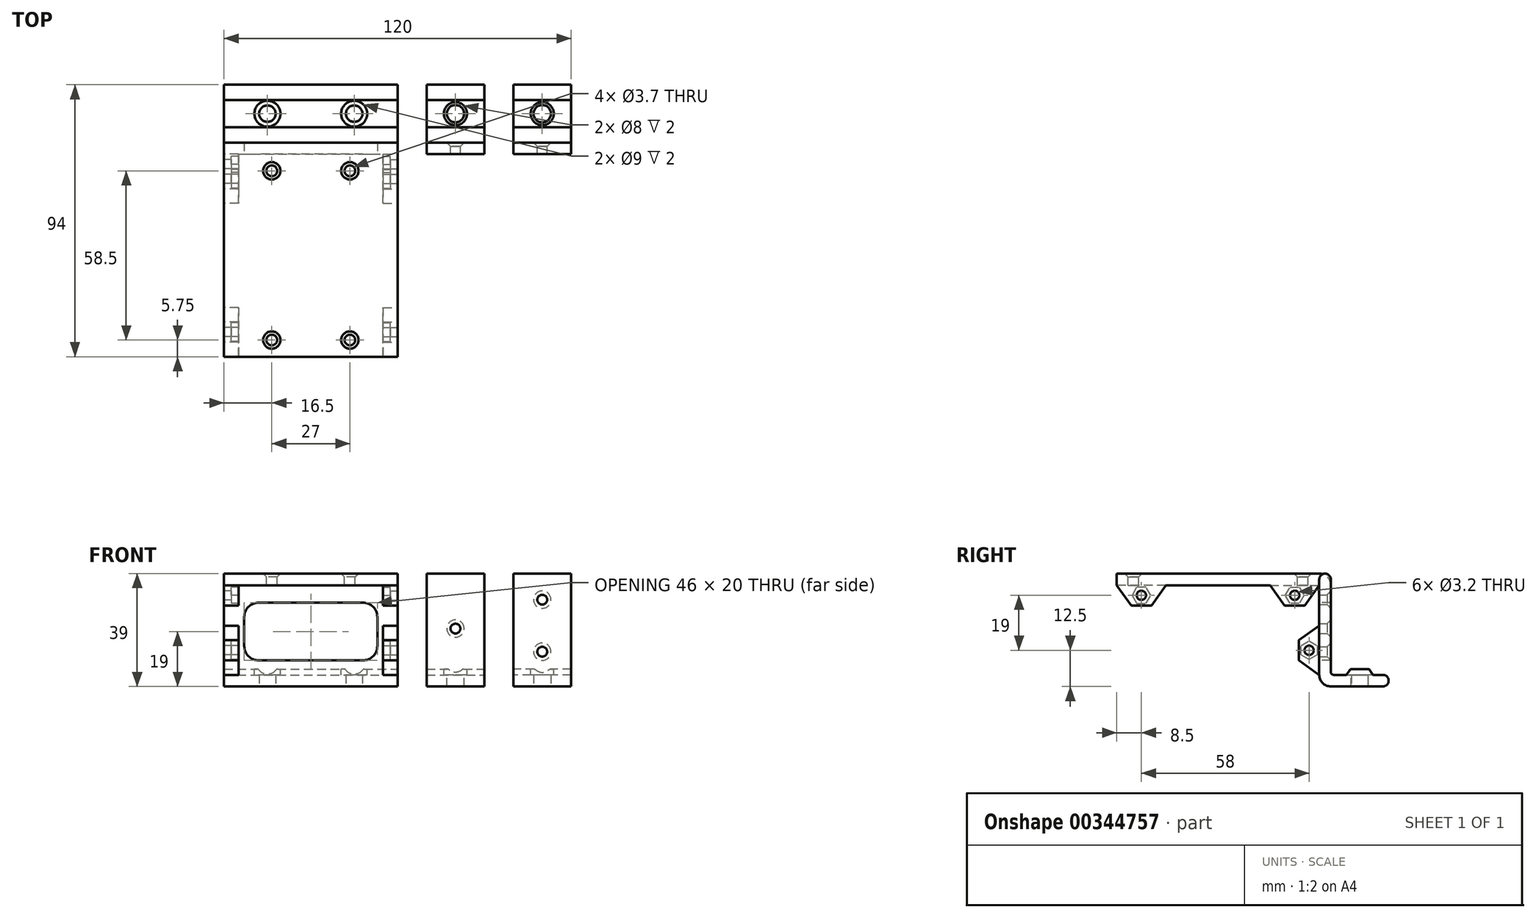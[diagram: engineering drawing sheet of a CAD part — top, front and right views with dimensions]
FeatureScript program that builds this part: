
annotation { "Feature Type Name" : "Feature", "Feature Type Description" : "" }
export const myFeature = defineFeature(function(context is Context, id is Id, definition is map)
    precondition{}
    {
        {
            var Q0;
            Q0=qCreatedBy(makeId("Right.planeOp"),FACE);
            var sketch = newSketch(context, id + "F0", { "sketchPlane" : qUnion([Q0])});
            skLineSegment(sketch, "E0", {"start": v(1, 0) * mm, "end": v(18, 0) * mm});
            skLineSegment(sketch, "E1", {"start": v(0, 1) * mm, "end": v(0, 33) * mm});
            skLineSegment(sketch, "E2.0", {"start": v(-4, 0) * mm, "end": v(-4, 33) * mm});
            skLineSegment(sketch, "E3.0", {"start": v(0, -4) * mm, "end": v(18, -4) * mm});
            skPoint(sketch, "E4.visualSharp", {"position": v(0, 0) * mm});
            skArc(sketch, "E4.filletArc", {"start": v(0, 1) * mm, "mid": v(0.3, 0.3) * mm, "end": v(1, 0) * mm});
            skArc(sketch, "E5", {"start": v(-4, 0) * mm, "mid": v(-2.83, -2.83) * mm, "end": v(0, -4) * mm});
            skLineSegment(sketch, "E6", {"start": v(31.11, 0) * mm, "end": v(-13.26, 0) * mm, "construction": true});
            skLineSegment(sketch, "E7", {"start": v(0, 49.75) * mm, "end": v(0, -11.4) * mm, "construction": true});
            skLineSegment(sketch, "E8", {"start": v(20, -2) * mm, "end": v(20, -2) * mm});
            skPoint(sketch, "E9.visualSharp", {"position": v(20, 0) * mm});
            skArc(sketch, "E9.filletArc", {"start": v(20, -2) * mm, "mid": v(19.41, -0.59) * mm, "end": v(18, 0) * mm});
            skPoint(sketch, "E10.visualSharp", {"position": v(20, -4) * mm});
            skArc(sketch, "E10.filletArc", {"start": v(18, -4) * mm, "mid": v(19.41, -3.41) * mm, "end": v(20, -2) * mm});
            skLineSegment(sketch, "E11", {"start": v(-2, 35) * mm, "end": v(-2, 35) * mm});
            skPoint(sketch, "E12.visualSharp", {"position": v(-4, 35) * mm});
            skArc(sketch, "E12.filletArc", {"start": v(-2, 35) * mm, "mid": v(-3.41, 34.41) * mm, "end": v(-4, 33) * mm});
            skPoint(sketch, "E13.visualSharp", {"position": v(0, 35) * mm});
            skArc(sketch, "E13.filletArc", {"start": v(0, 33) * mm, "mid": v(-0.59, 34.41) * mm, "end": v(-2, 35) * mm});
            skLineSegment(sketch, "E14", {"start": v(14.65, 0) * mm, "end": v(13.3, 1.8) * mm});
            skLineSegment(sketch, "E15", {"start": v(12.9, 2) * mm, "end": v(10, 2) * mm});
            skLineSegment(sketch, "E16.MirrorCS", {"start": v(7.1, 2) * mm, "end": v(10, 2) * mm});
            skLineSegment(sketch, "E17.MirrorCS", {"start": v(5.35, 0) * mm, "end": v(6.7, 1.8) * mm});
            skPoint(sketch, "E18.visualSharp", {"position": v(13.15, 2) * mm});
            skArc(sketch, "E18.filletArc", {"start": v(13.3, 1.8) * mm, "mid": v(13.12, 1.95) * mm, "end": v(12.9, 2) * mm});
            skPoint(sketch, "E19.visualSharp", {"position": v(6.85, 2) * mm});
            skArc(sketch, "E19.filletArc", {"start": v(7.1, 2) * mm, "mid": v(6.88, 1.95) * mm, "end": v(6.7, 1.8) * mm});
            skSolve(sketch);
        }
        {
            var Q0;
            Q0 = qSketchRegion(id + "F0", true);
            extrude(context, id + "F1", {"entities" : qUnion([Q0]), "depth" : 20 * mm});
        }
        {
            var Q0;
            Q0=makeQuery(id+"F1.opExtrude","SWEPT_FACE",FACE,{"disambiguationData":[OSD([sQuery(id+"F0.wireOp",EDGE,"E3.0")])]});
            var sketch = newSketch(context, id + "F2", { "sketchPlane" : qUnion([Q0])});
            skLineSegment(sketch, "E20.0", {"start": v(20, 0) * mm, "end": v(0, 0) * mm, "construction": true});
            skLineSegment(sketch, "E21.0", {"start": v(20, -18) * mm, "end": v(0, -18) * mm, "construction": true});
            skLineSegment(sketch, "E22.0", {"start": v(20, 0) * mm, "end": v(20, -18) * mm, "construction": true});
            skLineSegment(sketch, "E23.0", {"start": v(0, 0) * mm, "end": v(0, -18) * mm, "construction": true});
            skCircle(sketch, "E24", {"center": v(10, -10) * mm, "radius": 3 * mm});
            skSolve(sketch);
        }
        {
            var Q0;
            Q0=makeQuery(id+"F2.imprint","IMPRINT",FACE,{"disambiguationData":[TD([[makeQuery(id+"F2.imprint","IMPRINT",EDGE,{"derivedFrom":sQuery(id+"F2.wireOp",EDGE,"E24")}),1.0]])]});
            extrude(context, id + "F3", {"entities" : qUnion([Q0]), "operationType" : NewBodyOperationType.REMOVE, "endBound" : BoundingType.UP_TO_NEXT, "oppositeDirection" : true, "depth" : 25 * mm});
        }
        {
            var Q0;
            {var subQ0=sQuery(id+"F0.wireOp",EDGE,"E19.filletArc");var subQ1=sQuery(id+"F0.wireOp",EDGE,"E18.filletArc");var subQ2=sQuery(id+"F0.wireOp",EDGE,"E16.MirrorCS");var subQ3=sQuery(id+"F0.wireOp",EDGE,"E15");Q0=makeQuery(id+"F3.boolean.opBoolean","SPLIT",FACE,{"disambiguationData":[TD([makeQuery(id+"F1.opExtrude","CAP_FACE",FACE,{"disambiguationData":[OSD([sQuery(id+"F0.wireOp",EDGE,"E0"),sQuery(id+"F0.wireOp",EDGE,"E1"),sQuery(id+"F0.wireOp",EDGE,"E2.0"),sQuery(id+"F0.wireOp",EDGE,"E3.0"),sQuery(id+"F0.wireOp",EDGE,"E4.filletArc"),sQuery(id+"F0.wireOp",EDGE,"E5"),sQuery(id+"F0.wireOp",EDGE,"E9.filletArc"),sQuery(id+"F0.wireOp",EDGE,"E10.filletArc"),sQuery(id+"F0.wireOp",EDGE,"E12.filletArc"),sQuery(id+"F0.wireOp",EDGE,"E13.filletArc"),sQuery(id+"F0.wireOp",EDGE,"E14"),subQ3,subQ2,sQuery(id+"F0.wireOp",EDGE,"E17.MirrorCS"),subQ1,subQ0])],"isStart":false})])],"derivedFrom":makeQuery(id+"F1.opExtrude","SWEPT_FACE",FACE,{"disambiguationData":[OSD([subQ3,subQ2])]})});}
            var sketch = newSketch(context, id + "F4", { "sketchPlane" : qUnion([Q0])});
            skPoint(sketch, "E25.0", {"position": v(10, 10) * mm});
            skCircle(sketch, "E26", {"center": v(10, 10) * mm, "radius": 4 * mm});
            skSolve(sketch);
        }
        {
            var Q0;
            Q0=makeQuery(id+"F1.opExtrude","SWEPT_FACE",FACE,{"disambiguationData":[OSD([sQuery(id+"F0.wireOp",EDGE,"E2.0")])]});
            var sketch = newSketch(context, id + "F5", { "sketchPlane" : qUnion([Q0])});
            skLineSegment(sketch, "E27", {"start": v(0, 35) * mm, "end": v(20, 35) * mm, "construction": true});
            skLineSegment(sketch, "E28.0", {"start": v(0, 0) * mm, "end": v(0, 33) * mm, "construction": true});
            skCircle(sketch, "E29", {"center": v(10, 26) * mm, "radius": 1.85 * mm});
            skLineSegment(sketch, "E30.0", {"start": v(20, 0) * mm, "end": v(0, 0) * mm, "construction": true});
            skCircle(sketch, "E31", {"center": v(10, 8) * mm, "radius": 1.85 * mm});
            skSolve(sketch);
        }
        {
            var Q0;
            Q0=makeQuery(id+"F1.opExtrude","SWEPT_FACE",FACE,{"disambiguationData":[OSD([sQuery(id+"F0.wireOp",EDGE,"E1")])]});
            var sketch = newSketch(context, id + "F6", { "sketchPlane" : qUnion([Q0])});
            skPoint(sketch, "E32.0", {"position": v(-10, 26) * mm});
            skPoint(sketch, "E33.0", {"position": v(-10, 8) * mm});
            skSolve(sketch);
        }
        {
            var Q0;
            Q0=sQuery(id+"F6.wireOp",VERTEX,"E32.0");
            var Q1;
            Q1=sQuery(id+"F6.wireOp",VERTEX,"E33.0");
            var Q2;
            Q2=makeQuery(id+"F1.opExtrude","SWEPT_BODY",BODY,{"disambiguationData":[OSD([sQuery(id+"F0.wireOp",EDGE,"E0"),sQuery(id+"F0.wireOp",EDGE,"E1"),sQuery(id+"F0.wireOp",EDGE,"E2.0"),sQuery(id+"F0.wireOp",EDGE,"E3.0"),sQuery(id+"F0.wireOp",EDGE,"E4.filletArc"),sQuery(id+"F0.wireOp",EDGE,"E5"),sQuery(id+"F0.wireOp",EDGE,"E9.filletArc"),sQuery(id+"F0.wireOp",EDGE,"E10.filletArc"),sQuery(id+"F0.wireOp",EDGE,"E12.filletArc"),sQuery(id+"F0.wireOp",EDGE,"E13.filletArc")])]});
            hole(context, id + "F7", {"style" : HoleStyle.C_SINK, "endStyle" : HoleEndStyle.BLIND, "holeDiameter" : 3.4 * mm, "cSinkDiameter" : 6 * mm, "cSinkAngle" : 90 * degree, "holeDepth" : 12 * mm, "isTappedThrough" : true, "tappedDepth" : 12 * mm, "tapClearance" : 3, "locations" : qUnion([Q0, Q1]), "scope" : qUnion([Q2])});
        }
        {
            var Q0;
            Q0=qCreatedBy(makeId("Right.planeOp"),FACE);
            cPlane(context, id + "F8", {"entities" : qUnion([Q0]), "cplaneType" : CPlaneType.OFFSET, "offset" : 10 * mm, "oppositeDirection" : true, "width" : 150 * mm, "height" : 150 * mm});
        }
        {
            var Q0;
            Q0=qCreatedBy(id+"F8.planeOp",FACE);
            var sketch = newSketch(context, id + "F9", { "sketchPlane" : qUnion([Q0])});
            skPoint(sketch, "E34.0", {"position": v(-0.59, 34.41) * mm});
            skLineSegment(sketch, "E35.0", {"start": v(0, 1) * mm, "end": v(0, 33) * mm});
            skArc(sketch, "E35.1", {"start": v(0, 33) * mm, "mid": v(-0.59, 34.41) * mm, "end": v(-2, 35) * mm});
            skPoint(sketch, "E35.2", {"position": v(-4, 33) * mm});
            skLineSegment(sketch, "E35.3", {"start": v(-4, 0) * mm, "end": v(-4, 33) * mm});
            skArc(sketch, "E35.4", {"start": v(-2, 35) * mm, "mid": v(-3.41, 34.41) * mm, "end": v(-4, 33) * mm});
            skPoint(sketch, "E35.5", {"position": v(-3.41, 34.41) * mm});
            skLineSegment(sketch, "E36.0", {"start": v(1, 0) * mm, "end": v(18, 0) * mm});
            skPoint(sketch, "E37.0", {"position": v(19.41, -0.59) * mm});
            skPoint(sketch, "E38.0", {"position": v(19.41, -3.41) * mm});
            skArc(sketch, "E39.0", {"start": v(20, -2) * mm, "mid": v(19.41, -0.59) * mm, "end": v(18, 0) * mm});
            skArc(sketch, "E40.0", {"start": v(18, -4) * mm, "mid": v(19.41, -3.41) * mm, "end": v(20, -2) * mm});
            skLineSegment(sketch, "E41.0", {"start": v(0, -4) * mm, "end": v(18, -4) * mm});
            skArc(sketch, "E42.0", {"start": v(-4, 0) * mm, "mid": v(-2.83, -2.83) * mm, "end": v(0, -4) * mm});
            skArc(sketch, "E43.0", {"start": v(0, 1) * mm, "mid": v(0.3, 0.3) * mm, "end": v(1, 0) * mm});
            skLineSegment(sketch, "E44.0", {"start": v(14.65, 0) * mm, "end": v(13.3, 1.8) * mm});
            skArc(sketch, "E45.0", {"start": v(13.3, 1.8) * mm, "mid": v(13.12, 1.95) * mm, "end": v(12.9, 2) * mm});
            skLineSegment(sketch, "E46.0", {"start": v(12.9, 2) * mm, "end": v(10, 2) * mm});
            skLineSegment(sketch, "E47.0", {"start": v(7.1, 2) * mm, "end": v(10, 2) * mm});
            skArc(sketch, "E48.0", {"start": v(7.1, 2) * mm, "mid": v(6.88, 1.95) * mm, "end": v(6.7, 1.8) * mm});
            skLineSegment(sketch, "E49.0", {"start": v(5.35, 0) * mm, "end": v(6.7, 1.8) * mm});
            skSolve(sketch);
        }
        {
            var Q0;
            Q0=makeQuery(id+"F9.imprint","IMPRINT",FACE,{"disambiguationData":[TD([[makeQuery(id+"F9.imprint","IMPRINT",EDGE,{"derivedFrom":sQuery(id+"F9.wireOp",EDGE,"E35.0")}),1.0]])]});
            var Q1;
            {var subQ0=sQuery(id+"F9.wireOp",EDGE,"E44.0");Q1=makeQuery(id+"F9.imprint","IMPRINT",FACE,{"disambiguationData":[TD([[makeQuery(id+"F9.imprint","IMPRINT",EDGE,{"derivedFrom":subQ0}),1.0]])]});}
            extrude(context, id + "F10", {"entities" : qUnion([Q0, Q1]), "oppositeDirection" : true, "depth" : 20 * mm});
        }
        {
            var Q0;
            Q0=makeQuery(id+"F10.opExtrude","SWEPT_FACE",FACE,{"disambiguationData":[OSD([sQuery(id+"F9.wireOp",EDGE,"E36.0")])]});
            var sketch = newSketch(context, id + "F11", { "sketchPlane" : qUnion([Q0])});
            skCircle(sketch, "E50", {"center": v(-20, 10) * mm, "radius": 3 * mm});
            skLineSegment(sketch, "E51.0", {"start": v(-30, 0) * mm, "end": v(-10, 0) * mm, "construction": true});
            skSolve(sketch);
        }
        {
            var Q0;
            Q0=makeQuery(id+"F11.imprint","IMPRINT",FACE,{"disambiguationData":[TD([[makeQuery(id+"F11.imprint","IMPRINT",EDGE,{"derivedFrom":sQuery(id+"F11.wireOp",EDGE,"E50")}),1.0]])]});
            extrude(context, id + "F12", {"entities" : qUnion([Q0]), "operationType" : NewBodyOperationType.REMOVE, "endBound" : BoundingType.SYMMETRIC, "oppositeDirection" : true, "depth" : 25 * mm});
        }
        {
            var Q0;
            {var subQ0=sQuery(id+"F9.wireOp",EDGE,"E48.0");var subQ1=sQuery(id+"F9.wireOp",EDGE,"E47.0");var subQ2=sQuery(id+"F9.wireOp",EDGE,"E46.0");var subQ3=sQuery(id+"F9.wireOp",EDGE,"E45.0");Q0=makeQuery(id+"F12.boolean.opBoolean","SPLIT",FACE,{"disambiguationData":[TD([makeQuery(id+"F10.opExtrude","CAP_FACE",FACE,{"disambiguationData":[OSD([sQuery(id+"F9.wireOp",EDGE,"E35.0"),sQuery(id+"F9.wireOp",EDGE,"E35.1"),sQuery(id+"F9.wireOp",EDGE,"E35.3"),sQuery(id+"F9.wireOp",EDGE,"E35.4"),sQuery(id+"F9.wireOp",EDGE,"E36.0"),sQuery(id+"F9.wireOp",EDGE,"E39.0"),sQuery(id+"F9.wireOp",EDGE,"E40.0"),sQuery(id+"F9.wireOp",EDGE,"E41.0"),sQuery(id+"F9.wireOp",EDGE,"E42.0"),sQuery(id+"F9.wireOp",EDGE,"E43.0"),sQuery(id+"F9.wireOp",EDGE,"E44.0"),subQ3,subQ2,subQ1,subQ0,sQuery(id+"F9.wireOp",EDGE,"E49.0")])],"isStart":true})])],"derivedFrom":makeQuery(id+"F10.opExtrude","SWEPT_FACE",FACE,{"disambiguationData":[OSD([subQ2,subQ1])]})});}
            var sketch = newSketch(context, id + "F13", { "sketchPlane" : qUnion([Q0])});
            skPoint(sketch, "E52.0", {"position": v(-20, 10) * mm});
            skCircle(sketch, "E53", {"center": v(-20, 10) * mm, "radius": 4 * mm});
            skSolve(sketch);
        }
        {
            var Q0;
            Q0 = qSketchRegion(id + "F13", true);
            extrude(context, id + "F14", {"entities" : qUnion([Q0]), "operationType" : NewBodyOperationType.REMOVE, "oppositeDirection" : true, "depth" : 2 * mm});
        }
        {
            var Q0;
            Q0=makeQuery(id+"F10.opExtrude","SWEPT_FACE",FACE,{"disambiguationData":[OSD([sQuery(id+"F9.wireOp",EDGE,"E35.0")])]});
            var sketch = newSketch(context, id + "F15", { "sketchPlane" : qUnion([Q0])});
            skLineSegment(sketch, "E54.0", {"start": v(30, 0) * mm, "end": v(10, 0) * mm, "construction": true});
            skPoint(sketch, "E55", {"position": v(20, 16) * mm});
            skSolve(sketch);
        }
        {
            var Q0;
            Q0=sQuery(id+"F15.wireOp",VERTEX,"E55");
            var Q1;
            Q1=makeQuery(id+"F10.opExtrude","SWEPT_BODY",BODY,{"disambiguationData":[OSD([sQuery(id+"F9.wireOp",EDGE,"E35.0"),sQuery(id+"F9.wireOp",EDGE,"E35.1"),sQuery(id+"F9.wireOp",EDGE,"E35.3"),sQuery(id+"F9.wireOp",EDGE,"E35.4"),sQuery(id+"F9.wireOp",EDGE,"E36.0"),sQuery(id+"F9.wireOp",EDGE,"E39.0"),sQuery(id+"F9.wireOp",EDGE,"E40.0"),sQuery(id+"F9.wireOp",EDGE,"E41.0"),sQuery(id+"F9.wireOp",EDGE,"E42.0"),sQuery(id+"F9.wireOp",EDGE,"E43.0")])]});
            hole(context, id + "F16", {"style" : HoleStyle.C_SINK, "endStyle" : HoleEndStyle.BLIND, "holeDiameter" : 3.4 * mm, "cSinkDiameter" : 6 * mm, "cSinkAngle" : 90 * degree, "holeDepth" : 12 * mm, "isTappedThrough" : true, "tappedDepth" : 12 * mm, "tapClearance" : 3, "locations" : qUnion([Q0]), "scope" : qUnion([Q1])});
        }
        {
            var Q0;
            Q0=qCreatedBy(makeId("Right.planeOp"),FACE);
            cPlane(context, id + "F17", {"entities" : qUnion([Q0]), "cplaneType" : CPlaneType.OFFSET, "offset" : 40 * mm, "oppositeDirection" : true, "width" : 150 * mm, "height" : 150 * mm});
        }
        {
            var Q0;
            Q0=qCreatedBy(id+"F17.planeOp",FACE);
            var sketch = newSketch(context, id + "F18", { "sketchPlane" : qUnion([Q0])});
            skLineSegment(sketch, "E56.0.2", {"start": v(-4, 35) * mm, "end": v(-4, 0) * mm});
            skArc(sketch, "E56.0.3", {"start": v(-4, 0) * mm, "mid": v(-2.83, -2.83) * mm, "end": v(0, -4) * mm});
            skLineSegment(sketch, "E56.0.4", {"start": v(0, -4) * mm, "end": v(18, -4) * mm});
            skArc(sketch, "E56.0.5", {"start": v(18, -4) * mm, "mid": v(19.41, -3.41) * mm, "end": v(20, -2) * mm});
            skArc(sketch, "E56.0.6", {"start": v(20, -2) * mm, "mid": v(19.41, -0.59) * mm, "end": v(18, 0) * mm});
            skLineSegment(sketch, "E56.0.7", {"start": v(18, 0) * mm, "end": v(1, 0) * mm});
            skArc(sketch, "E56.0.8", {"start": v(1, 0) * mm, "mid": v(0.3, 0.3) * mm, "end": v(0, 1) * mm});
            skLineSegment(sketch, "E56.0.9", {"start": v(0, 1) * mm, "end": v(0, 35) * mm});
            skLineSegment(sketch, "E57", {"start": v(0, 35) * mm, "end": v(-4, 35) * mm});
            skLineSegment(sketch, "E58", {"start": v(10, -6.98) * mm, "end": v(10, 10.98) * mm, "construction": true});
            skPoint(sketch, "E58.startSnap0", {"position": v(10, -4) * mm});
            skLineSegment(sketch, "E59", {"start": v(14.65, 0) * mm, "end": v(13.3, 1.8) * mm});
            skLineSegment(sketch, "E60", {"start": v(12.9, 2) * mm, "end": v(10, 2) * mm});
            skLineSegment(sketch, "E61.MirrorCS", {"start": v(7.1, 2) * mm, "end": v(10, 2) * mm});
            skLineSegment(sketch, "E62.MirrorCS", {"start": v(5.35, 0) * mm, "end": v(6.7, 1.8) * mm});
            skPoint(sketch, "E63.visualSharp", {"position": v(13.15, 2) * mm});
            skArc(sketch, "E63.filletArc", {"start": v(13.3, 1.8) * mm, "mid": v(13.12, 1.95) * mm, "end": v(12.9, 2) * mm});
            skPoint(sketch, "E64.visualSharp", {"position": v(6.85, 2) * mm});
            skArc(sketch, "E64.filletArc", {"start": v(7.1, 2) * mm, "mid": v(6.88, 1.95) * mm, "end": v(6.7, 1.8) * mm});
            skSolve(sketch);
        }
        {
            var Q0;
            Q0=makeQuery(id+"F18.imprint","IMPRINT",FACE,{"disambiguationData":[TD([[makeQuery(id+"F18.imprint","IMPRINT",EDGE,{"derivedFrom":sQuery(id+"F18.wireOp",EDGE,"E56.0.2")}),1.0]])]});
            var Q1;
            {var subQ0=sQuery(id+"F18.wireOp",EDGE,"E59");Q1=makeQuery(id+"F18.imprint","IMPRINT",FACE,{"disambiguationData":[TD([[makeQuery(id+"F18.imprint","IMPRINT",EDGE,{"derivedFrom":subQ0}),1.0]])]});}
            extrude(context, id + "F19", {"entities" : qUnion([Q0, Q1]), "operationType" : NewBodyOperationType.ADD, "oppositeDirection" : true, "depth" : 60 * mm});
        }
        {
            var Q0;
            Q0=makeQuery(id+"F19.opExtrude","SWEPT_FACE",FACE,{"disambiguationData":[OSD([sQuery(id+"F18.wireOp",EDGE,"E57")])]});
            var sketch = newSketch(context, id + "F20", { "sketchPlane" : qUnion([Q0])});
            skLineSegment(sketch, "E65.0", {"start": v(-100, -4) * mm, "end": v(-40, -4) * mm});
            skLineSegment(sketch, "E66.top", {"start": v(-100, -74) * mm, "end": v(-40, -74) * mm});
            skLineSegment(sketch, "E66.left", {"start": v(-100, -4) * mm, "end": v(-100, -74) * mm});
            skLineSegment(sketch, "E66.right", {"start": v(-40, -4) * mm, "end": v(-40, -74) * mm});
            skSolve(sketch);
        }
        {
            var Q0;
            Q0 = qSketchRegion(id + "F20", true);
            extrude(context, id + "F21", {"entities" : qUnion([Q0]), "operationType" : NewBodyOperationType.ADD, "oppositeDirection" : true, "depth" : 4 * mm});
        }
        {
            var Q0;
            Q0=makeQuery(id+"F19.opExtrude","SWEPT_EDGE",EDGE,{"disambiguationData":[OSD([sQuery(id+"F18.wireOp",EDGE,"E56.0.9"),sQuery(id+"F18.wireOp",EDGE,"E57")])]});
            fillet(context, id + "F22", {"entities" : qUnion([Q0]), "radius" : 4 * mm, "tangentPropagation" : true, "allowEdgeOverflow" : false});
        }
        {
            var Q0;
            Q0=makeQuery(id+"F19.opExtrude","SWEPT_FACE",FACE,{"disambiguationData":[OSD([sQuery(id+"F18.wireOp",EDGE,"E56.0.4")])]});
            var sketch = newSketch(context, id + "F23", { "sketchPlane" : qUnion([Q0])});
            skLineSegment(sketch, "E67.0", {"start": v(-100, 0) * mm, "end": v(-100, -18) * mm, "construction": true});
            skLineSegment(sketch, "E68.0", {"start": v(-40, 0) * mm, "end": v(-40, -18) * mm, "construction": true});
            skPoint(sketch, "E69", {"position": v(-85, -10) * mm});
            skLineSegment(sketch, "E70", {"start": v(-70, -20) * mm, "end": v(-70, 0) * mm, "construction": true});
            skLineSegment(sketch, "E71", {"start": v(-70, -10) * mm, "end": v(-100, -10) * mm, "construction": true});
            skLineSegment(sketch, "E72", {"start": v(-40, -20) * mm, "end": v(-100, -20) * mm, "construction": true});
            skLineSegment(sketch, "E73", {"start": v(-100, -20) * mm, "end": v(-100, 0) * mm, "construction": true});
            skPoint(sketch, "E74.MirrorP", {"position": v(-55, -10) * mm});
            skSolve(sketch);
        }
        {
            var Q0;
            Q0=sQuery(id+"F23.wireOp",VERTEX,"E69");
            var Q1;
            Q1=sQuery(id+"F23.wireOp",VERTEX,"E74.MirrorP");
            var Q2;
            Q2=makeQuery(id+"F19.opExtrude","SWEPT_BODY",BODY,{"disambiguationData":[OSD([sQuery(id+"F18.wireOp",EDGE,"E56.0.2"),sQuery(id+"F18.wireOp",EDGE,"E56.0.3"),sQuery(id+"F18.wireOp",EDGE,"E56.0.4"),sQuery(id+"F18.wireOp",EDGE,"E56.0.5"),sQuery(id+"F18.wireOp",EDGE,"E56.0.6"),sQuery(id+"F18.wireOp",EDGE,"E56.0.7"),sQuery(id+"F18.wireOp",EDGE,"E56.0.8"),sQuery(id+"F18.wireOp",EDGE,"E56.0.9"),sQuery(id+"F18.wireOp",EDGE,"E57"),sQuery(id+"F18.wireOp",EDGE,"E59"),sQuery(id+"F18.wireOp",EDGE,"E60"),sQuery(id+"F18.wireOp",EDGE,"E61.MirrorCS"),sQuery(id+"F18.wireOp",EDGE,"E62.MirrorCS")])]});
            hole(context, id + "F24", {"style" : HoleStyle.SIMPLE, "endStyle" : HoleEndStyle.THROUGH, "holeDiameter" : 5.7 * mm, "isTappedThrough" : true, "tappedDepth" : 12 * mm, "tapClearance" : 3, "locations" : qUnion([Q0, Q1]), "scope" : qUnion([Q2])});
        }
        {
            var Q0;
            {var subQ4=makeQuery(id+"F24.hole-0.opRevolve","SWEPT_FACE",FACE,{"disambiguationData":[OSD([sQuery(id+"F24.hole-0.sketch.wireOp",EDGE,"core_line_2")])]});var subQ5=sQuery(id+"F18.wireOp",EDGE,"E61.MirrorCS");var subQ6=sQuery(id+"F18.wireOp",EDGE,"E60");Q0=makeQuery(id+"F24.hole-1.boolean.opBoolean","SPLIT",FACE,{"disambiguationData":[TD([makeQuery(id+"F24.hole-0.boolean.opBoolean","COPY",FACE,{"derivedFrom":subQ4})])],"derivedFrom":makeQuery(id+"F24.hole-0.boolean.opBoolean","SPLIT",FACE,{"disambiguationData":[TD([makeQuery(id+"F21.opExtrude","SWEPT_FACE",FACE,{"disambiguationData":[OSD([sQuery(id+"F20.wireOp",EDGE,"E66.right")])]})])],"derivedFrom":makeQuery(id+"F19.opExtrude","SWEPT_FACE",FACE,{"disambiguationData":[OSD([subQ6,subQ5])]})})});}
            var sketch = newSketch(context, id + "F25", { "sketchPlane" : qUnion([Q0])});
            skCircle(sketch, "E75.0", {"center": v(-85, 10) * mm, "radius": 2.85 * mm});
            skCircle(sketch, "E76.0", {"center": v(-55, 10) * mm, "radius": 2.85 * mm});
            skCircle(sketch, "E77", {"center": v(-85, 10) * mm, "radius": 4.5 * mm});
            skCircle(sketch, "E78", {"center": v(-55, 10) * mm, "radius": 4.5 * mm});
            skSolve(sketch);
        }
        {
            var Q0;
            {var subQ0=sQuery(id+"F25.wireOp",EDGE,"E75.0");Q0=makeQuery(id+"F25.imprint","IMPRINT",FACE,{"disambiguationData":[TD([[makeQuery(id+"F25.imprint","IMPRINT",EDGE,{"disambiguationData":[OD(1.0)],"derivedFrom":subQ0}),1.0]])]});}
            var Q1;
            {var subQ0=sQuery(id+"F25.wireOp",EDGE,"E77");var subQ1=makeQuery(id+"F19.opExtrude","SWEPT_EDGE",EDGE,{"disambiguationData":[OSD([sQuery(id+"F18.wireOp",EDGE,"E60"),sQuery(id+"F18.wireOp",EDGE,"E63.filletArc")])]});var subQ2=makeQuery(id+"F25.imprint","INTERSECT",VERTEX,{"disambiguationData":[OD(0.0)],"derivedFrom":[subQ1,subQ0]});Q1=makeQuery(id+"F25.imprint","IMPRINT",FACE,{"disambiguationData":[TD([[makeQuery(id+"F25.imprint","IMPRINT",EDGE,{"disambiguationData":[TD([[subQ2,1.0]])],"derivedFrom":subQ0}),1.0]])]});}
            var Q2;
            {var subQ0=sQuery(id+"F25.wireOp",EDGE,"E75.0");Q2=makeQuery(id+"F25.imprint","IMPRINT",FACE,{"disambiguationData":[TD([[makeQuery(id+"F25.imprint","IMPRINT",EDGE,{"disambiguationData":[OD(0.0)],"derivedFrom":subQ0}),-1.0]])]});}
            var Q3;
            {var subQ0=sQuery(id+"F25.wireOp",EDGE,"E76.0");Q3=makeQuery(id+"F25.imprint","IMPRINT",FACE,{"disambiguationData":[TD([[makeQuery(id+"F25.imprint","IMPRINT",EDGE,{"disambiguationData":[OD(0.0)],"derivedFrom":subQ0}),-1.0]])]});}
            var Q4;
            {var subQ0=sQuery(id+"F25.wireOp",EDGE,"E77");var subQ1=makeQuery(id+"F19.opExtrude","SWEPT_EDGE",EDGE,{"disambiguationData":[OSD([sQuery(id+"F18.wireOp",EDGE,"E61.MirrorCS"),sQuery(id+"F18.wireOp",EDGE,"E64.filletArc")])]});var subQ2=makeQuery(id+"F25.imprint","INTERSECT",VERTEX,{"disambiguationData":[OD(0.0)],"derivedFrom":[subQ1,subQ0]});Q4=makeQuery(id+"F25.imprint","IMPRINT",FACE,{"disambiguationData":[TD([[makeQuery(id+"F25.imprint","IMPRINT",EDGE,{"disambiguationData":[TD([[subQ2,-1.0]])],"derivedFrom":subQ0}),1.0]])]});}
            var Q5;
            Q5=makeQuery(id+"F25.imprint","IMPRINT",FACE,{"disambiguationData":[TD([[makeQuery(id+"F25.imprint","IMPRINT",EDGE,{"derivedFrom":sQuery(id+"F25.wireOp",EDGE,"E76.0")}),1.0]])]});
            var Q6;
            {var subQ0=sQuery(id+"F25.wireOp",EDGE,"E78");var subQ1=makeQuery(id+"F19.opExtrude","SWEPT_EDGE",EDGE,{"disambiguationData":[OSD([sQuery(id+"F18.wireOp",EDGE,"E61.MirrorCS"),sQuery(id+"F18.wireOp",EDGE,"E64.filletArc")])]});var subQ2=makeQuery(id+"F25.imprint","INTERSECT",VERTEX,{"disambiguationData":[OD(0.0)],"derivedFrom":[subQ1,subQ0]});Q6=makeQuery(id+"F25.imprint","IMPRINT",FACE,{"disambiguationData":[TD([[makeQuery(id+"F25.imprint","IMPRINT",EDGE,{"disambiguationData":[TD([[subQ2,-1.0]])],"derivedFrom":subQ0}),1.0]])]});}
            var Q7;
            {var subQ0=sQuery(id+"F25.wireOp",EDGE,"E78");var subQ1=makeQuery(id+"F19.opExtrude","SWEPT_EDGE",EDGE,{"disambiguationData":[OSD([sQuery(id+"F18.wireOp",EDGE,"E60"),sQuery(id+"F18.wireOp",EDGE,"E63.filletArc")])]});var subQ2=makeQuery(id+"F25.imprint","INTERSECT",VERTEX,{"disambiguationData":[OD(0.0)],"derivedFrom":[subQ1,subQ0]});Q7=makeQuery(id+"F25.imprint","IMPRINT",FACE,{"disambiguationData":[TD([[makeQuery(id+"F25.imprint","IMPRINT",EDGE,{"disambiguationData":[TD([[subQ2,1.0]])],"derivedFrom":subQ0}),1.0]])]});}
            var Q8;
            {var subQ0=sQuery(id+"F18.wireOp",EDGE,"E56.0.7");Q8=makeQuery(id+"F19.opExtrude","SWEPT_FACE",FACE,{"disambiguationData":[OSD([subQ0]),TDD([makeQuery(id+"F18.imprint","IMPRINT",EDGE,{"disambiguationData":[TD([[makeQuery(id+"F18.imprint","INTERSECT",VERTEX,{"derivedFrom":[sQuery(id+"F18.wireOp",EDGE,"E56.0.6"),subQ0]}),-1.0]])],"derivedFrom":subQ0})])]});}
            extrude(context, id + "F26", {"entities" : qUnion([Q0, Q1, Q2, Q3, Q4, Q5, Q6, Q7]), "operationType" : NewBodyOperationType.REMOVE, "endBound" : BoundingType.UP_TO_SURFACE, "oppositeDirection" : true, "endBoundEntityFace" : qUnion([Q8]), "depth" : 25 * mm});
        }
        {
            var Q0;
            Q0=makeQuery(id+"F21.boolean.opBoolean","MERGE",FACE,{"derivedFrom":[makeQuery(id+"F19.opExtrude","SWEPT_FACE",FACE,{"disambiguationData":[OSD([sQuery(id+"F18.wireOp",EDGE,"E57")])]}),makeQuery(id+"F21.opExtrude","CAP_FACE",FACE,{"disambiguationData":[OSD([sQuery(id+"F20.wireOp",EDGE,"E65.0"),sQuery(id+"F20.wireOp",EDGE,"E66.top"),sQuery(id+"F20.wireOp",EDGE,"E66.left"),sQuery(id+"F20.wireOp",EDGE,"E66.right")])],"isStart":true})]});
            var sketch = newSketch(context, id + "F27", { "sketchPlane" : qUnion([Q0])});
            skLineSegment(sketch, "E79", {"start": v(-56.5, -4) * mm, "end": v(-56.5, -74) * mm, "construction": true});
            skLineSegment(sketch, "E80", {"start": v(-83.5, -74) * mm, "end": v(-83.5, -4) * mm, "construction": true});
            skLineSegment(sketch, "E81", {"start": v(-100, -68.25) * mm, "end": v(-40, -68.25) * mm, "construction": true});
            skLineSegment(sketch, "E82", {"start": v(-40, -9.75) * mm, "end": v(-100, -9.75) * mm, "construction": true});
            skPoint(sketch, "E83", {"position": v(-83.5, -68.25) * mm});
            skPoint(sketch, "E84", {"position": v(-56.5, -68.25) * mm});
            skPoint(sketch, "E85", {"position": v(-56.5, -9.75) * mm});
            skPoint(sketch, "E86", {"position": v(-83.5, -9.75) * mm});
            skSolve(sketch);
        }
        {
            var Q0;
            Q0=sQuery(id+"F27.wireOp",VERTEX,"E86");
            var Q1;
            Q1=sQuery(id+"F27.wireOp",VERTEX,"E83");
            var Q2;
            Q2=sQuery(id+"F27.wireOp",VERTEX,"E84");
            var Q3;
            Q3=sQuery(id+"F27.wireOp",VERTEX,"E85");
            var Q4;
            Q4=makeQuery(id+"F19.opExtrude","SWEPT_BODY",BODY,{"disambiguationData":[OSD([sQuery(id+"F18.wireOp",EDGE,"E56.0.2"),sQuery(id+"F18.wireOp",EDGE,"E56.0.3"),sQuery(id+"F18.wireOp",EDGE,"E56.0.4"),sQuery(id+"F18.wireOp",EDGE,"E56.0.5"),sQuery(id+"F18.wireOp",EDGE,"E56.0.6"),sQuery(id+"F18.wireOp",EDGE,"E56.0.7"),sQuery(id+"F18.wireOp",EDGE,"E56.0.8"),sQuery(id+"F18.wireOp",EDGE,"E56.0.9"),sQuery(id+"F18.wireOp",EDGE,"E57"),sQuery(id+"F18.wireOp",EDGE,"E59"),sQuery(id+"F18.wireOp",EDGE,"E60"),sQuery(id+"F18.wireOp",EDGE,"E61.MirrorCS"),sQuery(id+"F18.wireOp",EDGE,"E62.MirrorCS")])]});
            hole(context, id + "F28", {"style" : HoleStyle.C_SINK, "endStyle" : HoleEndStyle.THROUGH, "holeDiameter" : 3.7 * mm, "cSinkDiameter" : 6 * mm, "cSinkAngle" : 90 * degree, "isTappedThrough" : true, "tappedDepth" : 12 * mm, "tapClearance" : 3, "locations" : qUnion([Q0, Q1, Q2, Q3]), "scope" : qUnion([Q4])});
        }
        {
            var Q0;
            Q0 = qSketchRegion(id + "F4", true);
            extrude(context, id + "F29", {"entities" : qUnion([Q0]), "operationType" : NewBodyOperationType.REMOVE, "oppositeDirection" : true, "depth" : 2 * mm});
        }
        {
            var Q0;
            Q0=makeQuery(id+"F19.opExtrude","SWEPT_FACE",FACE,{"disambiguationData":[OSD([sQuery(id+"F18.wireOp",EDGE,"E56.0.2")])]});
            var sketch = newSketch(context, id + "F30", { "sketchPlane" : qUnion([Q0])});
            skLineSegment(sketch, "E87.0", {"start": v(-100, 0) * mm, "end": v(-40, 0) * mm, "construction": true});
            skLineSegment(sketch, "E88.0", {"start": v(-45, 30) * mm, "end": v(-100, 30) * mm, "construction": true});
            skLineSegment(sketch, "E89.bottom", {"start": v(-52, 5) * mm, "end": v(-88, 5) * mm});
            skLineSegment(sketch, "E89.top", {"start": v(-52, 25) * mm, "end": v(-88, 25) * mm});
            skLineSegment(sketch, "E89.left", {"start": v(-47, 10) * mm, "end": v(-47, 20) * mm});
            skLineSegment(sketch, "E89.right", {"start": v(-93, 10) * mm, "end": v(-93, 20) * mm});
            skPoint(sketch, "E90.visualSharp", {"position": v(-93, 5) * mm});
            skArc(sketch, "E90.filletArc", {"start": v(-93, 10) * mm, "mid": v(-91.54, 6.46) * mm, "end": v(-88, 5) * mm});
            skPoint(sketch, "E91.visualSharp", {"position": v(-47, 5) * mm});
            skArc(sketch, "E91.filletArc", {"start": v(-52, 5) * mm, "mid": v(-48.46, 6.46) * mm, "end": v(-47, 10) * mm});
            skPoint(sketch, "E92.visualSharp", {"position": v(-47, 25) * mm});
            skArc(sketch, "E92.filletArc", {"start": v(-47, 20) * mm, "mid": v(-48.46, 23.54) * mm, "end": v(-52, 25) * mm});
            skPoint(sketch, "E93.visualSharp", {"position": v(-93, 25) * mm});
            skArc(sketch, "E93.filletArc", {"start": v(-88, 25) * mm, "mid": v(-91.54, 23.54) * mm, "end": v(-93, 20) * mm});
            skSolve(sketch);
        }
        {
            var Q0;
            Q0=makeQuery(id+"F30.imprint","IMPRINT",FACE,{"disambiguationData":[TD([[makeQuery(id+"F30.imprint","IMPRINT",EDGE,{"derivedFrom":sQuery(id+"F30.wireOp",EDGE,"E89.bottom")}),-1.0]])]});
            extrude(context, id + "F31", {"entities" : qUnion([Q0]), "operationType" : NewBodyOperationType.REMOVE, "oppositeDirection" : true, "depth" : 25 * mm});
        }
        {
            var Q0;
            Q0=makeQuery(id+"F21.boolean.opBoolean","MERGE",FACE,{"derivedFrom":[makeQuery(id+"F19.opExtrude","CAP_FACE",FACE,{"disambiguationData":[OSD([sQuery(id+"F18.wireOp",EDGE,"E56.0.2"),sQuery(id+"F18.wireOp",EDGE,"E56.0.3"),sQuery(id+"F18.wireOp",EDGE,"E56.0.4"),sQuery(id+"F18.wireOp",EDGE,"E56.0.5"),sQuery(id+"F18.wireOp",EDGE,"E56.0.6"),sQuery(id+"F18.wireOp",EDGE,"E56.0.7"),sQuery(id+"F18.wireOp",EDGE,"E56.0.8"),sQuery(id+"F18.wireOp",EDGE,"E56.0.9"),sQuery(id+"F18.wireOp",EDGE,"E57"),sQuery(id+"F18.wireOp",EDGE,"E59"),sQuery(id+"F18.wireOp",EDGE,"E60"),sQuery(id+"F18.wireOp",EDGE,"E61.MirrorCS"),sQuery(id+"F18.wireOp",EDGE,"E62.MirrorCS"),sQuery(id+"F18.wireOp",EDGE,"E63.filletArc"),sQuery(id+"F18.wireOp",EDGE,"E64.filletArc")])],"isStart":false}),makeQuery(id+"F21.opExtrude","SWEPT_FACE",FACE,{"disambiguationData":[OSD([sQuery(id+"F20.wireOp",EDGE,"E66.left")])]})]});
            var sketch = newSketch(context, id + "F32", { "sketchPlane" : qUnion([Q0])});
            skLineSegment(sketch, "E94", {"start": v(74, 31) * mm, "end": v(69, 24) * mm});
            skLineSegment(sketch, "E95", {"start": v(69, 24) * mm, "end": v(62, 24) * mm});
            skLineSegment(sketch, "E96", {"start": v(62, 24) * mm, "end": v(57, 31) * mm});
            skLineSegment(sketch, "E97", {"start": v(74, 31) * mm, "end": v(57, 31) * mm});
            skLineSegment(sketch, "E98", {"start": v(65.5, 24) * mm, "end": v(65.5, 31) * mm, "construction": true});
            skCircle(sketch, "E99", {"center": v(65.5, 27.5) * mm, "radius": 1.6 * mm});
            skCircle(sketch, "E100.cCircle", {"center": v(65.5, 27.5) * mm, "radius": 2.8 * mm, "construction": true});
            skLineSegment(sketch, "E100.0", {"start": v(67.12, 24.7) * mm, "end": v(63.88, 24.7) * mm});
            skLineSegment(sketch, "E100.1", {"start": v(63.88, 24.7) * mm, "end": v(62.27, 27.5) * mm});
            skLineSegment(sketch, "E100.2", {"start": v(62.27, 27.5) * mm, "end": v(63.88, 30.3) * mm});
            skLineSegment(sketch, "E100.3", {"start": v(63.88, 30.3) * mm, "end": v(67.12, 30.3) * mm});
            skLineSegment(sketch, "E100.4", {"start": v(67.12, 30.3) * mm, "end": v(68.73, 27.5) * mm});
            skLineSegment(sketch, "E100.5", {"start": v(68.73, 27.5) * mm, "end": v(67.12, 24.7) * mm});
            skPoint(sketch, "E100.0.midPoint", {"position": v(65.5, 24.7) * mm});
            skSolve(sketch);
        }
        {
            var Q0;
            Q0=makeQuery(id+"F32.imprint","IMPRINT",FACE,{"disambiguationData":[TD([[makeQuery(id+"F32.imprint","IMPRINT",EDGE,{"derivedFrom":sQuery(id+"F32.wireOp",EDGE,"E94")}),-1.0]])]});
            extrude(context, id + "F33", {"entities" : qUnion([Q0]), "oppositeDirection" : true, "depth" : 5 * mm});
        }
        {
            var Q0;
            Q0=makeQuery(id+"F32.imprint","IMPRINT",FACE,{"disambiguationData":[TD([[makeQuery(id+"F32.imprint","IMPRINT",EDGE,{"derivedFrom":sQuery(id+"F32.wireOp",EDGE,"E99")}),-1.0]])]});
            extrude(context, id + "F34", {"entities" : qUnion([Q0]), "operationType" : NewBodyOperationType.ADD, "oppositeDirection" : true, "depth" : 2.5 * mm});
        }
        {
            var Q0;
            Q0=makeQuery(id+"F21.boolean.opBoolean","MERGE",FACE,{"derivedFrom":[makeQuery(id+"F19.opExtrude","CAP_FACE",FACE,{"disambiguationData":[OSD([sQuery(id+"F18.wireOp",EDGE,"E56.0.2"),sQuery(id+"F18.wireOp",EDGE,"E56.0.3"),sQuery(id+"F18.wireOp",EDGE,"E56.0.4"),sQuery(id+"F18.wireOp",EDGE,"E56.0.5"),sQuery(id+"F18.wireOp",EDGE,"E56.0.6"),sQuery(id+"F18.wireOp",EDGE,"E56.0.7"),sQuery(id+"F18.wireOp",EDGE,"E56.0.8"),sQuery(id+"F18.wireOp",EDGE,"E56.0.9"),sQuery(id+"F18.wireOp",EDGE,"E57"),sQuery(id+"F18.wireOp",EDGE,"E59"),sQuery(id+"F18.wireOp",EDGE,"E60"),sQuery(id+"F18.wireOp",EDGE,"E61.MirrorCS"),sQuery(id+"F18.wireOp",EDGE,"E62.MirrorCS"),sQuery(id+"F18.wireOp",EDGE,"E63.filletArc"),sQuery(id+"F18.wireOp",EDGE,"E64.filletArc")])],"isStart":false}),makeQuery(id+"F21.opExtrude","SWEPT_FACE",FACE,{"disambiguationData":[OSD([sQuery(id+"F20.wireOp",EDGE,"E66.left")])]})]});
            var Q1;
            Q1=makeQuery(id+"F21.boolean.opBoolean","MERGE",FACE,{"derivedFrom":[makeQuery(id+"F19.opExtrude","CAP_FACE",FACE,{"disambiguationData":[OSD([sQuery(id+"F18.wireOp",EDGE,"E56.0.2"),sQuery(id+"F18.wireOp",EDGE,"E56.0.3"),sQuery(id+"F18.wireOp",EDGE,"E56.0.4"),sQuery(id+"F18.wireOp",EDGE,"E56.0.5"),sQuery(id+"F18.wireOp",EDGE,"E56.0.6"),sQuery(id+"F18.wireOp",EDGE,"E56.0.7"),sQuery(id+"F18.wireOp",EDGE,"E56.0.8"),sQuery(id+"F18.wireOp",EDGE,"E56.0.9"),sQuery(id+"F18.wireOp",EDGE,"E57"),sQuery(id+"F18.wireOp",EDGE,"E59"),sQuery(id+"F18.wireOp",EDGE,"E60"),sQuery(id+"F18.wireOp",EDGE,"E61.MirrorCS"),sQuery(id+"F18.wireOp",EDGE,"E62.MirrorCS"),sQuery(id+"F18.wireOp",EDGE,"E63.filletArc"),sQuery(id+"F18.wireOp",EDGE,"E64.filletArc")])],"isStart":true}),makeQuery(id+"F21.opExtrude","SWEPT_FACE",FACE,{"disambiguationData":[OSD([sQuery(id+"F20.wireOp",EDGE,"E66.right")])]})]});
            cPlane(context, id + "F35", {"entities" : qUnion([Q0, Q1]), "cplaneType" : CPlaneType.MID_PLANE, "offset" : 0 * mm, "width" : 150 * mm, "height" : 150 * mm});
        }
        {
            var Q0;
            Q0=makeQuery(id+"F33.opExtrude","SWEPT_BODY",BODY,{"disambiguationData":[OSD([sQuery(id+"F32.wireOp",EDGE,"E94"),sQuery(id+"F32.wireOp",EDGE,"E95"),sQuery(id+"F32.wireOp",EDGE,"E96"),sQuery(id+"F32.wireOp",EDGE,"E97"),sQuery(id+"F32.wireOp",EDGE,"E100.0"),sQuery(id+"F32.wireOp",EDGE,"E100.1"),sQuery(id+"F32.wireOp",EDGE,"E100.2"),sQuery(id+"F32.wireOp",EDGE,"E100.3"),sQuery(id+"F32.wireOp",EDGE,"E100.4"),sQuery(id+"F32.wireOp",EDGE,"E100.5")])]});
            var Q1;
            Q1=qCreatedBy(id+"F35.planeOp",FACE);
            mirror(context, id + "F36", {"entities" : qUnion([Q0]), "mirrorPlane" : qUnion([Q1])});
        }
        {
            var Q0;
            Q0=makeQuery(id+"F21.opExtrude","SWEPT_FACE",FACE,{"disambiguationData":[OSD([sQuery(id+"F20.wireOp",EDGE,"E66.top")])]});
            var Q1;
            Q1=makeQuery(id+"F19.opExtrude","SWEPT_FACE",FACE,{"disambiguationData":[OSD([sQuery(id+"F18.wireOp",EDGE,"E56.0.2")])]});
            cPlane(context, id + "F37", {"entities" : qUnion([Q0, Q1]), "cplaneType" : CPlaneType.MID_PLANE, "offset" : 25 * mm, "width" : 150 * mm, "height" : 150 * mm});
        }
        {
            var Q0;
            Q0=makeQuery(id+"F36.opPattern","COPY",BODY,{"derivedFrom":makeQuery(id+"F33.opExtrude","SWEPT_BODY",BODY,{"disambiguationData":[OSD([sQuery(id+"F32.wireOp",EDGE,"E94"),sQuery(id+"F32.wireOp",EDGE,"E95"),sQuery(id+"F32.wireOp",EDGE,"E96"),sQuery(id+"F32.wireOp",EDGE,"E97"),sQuery(id+"F32.wireOp",EDGE,"E100.0"),sQuery(id+"F32.wireOp",EDGE,"E100.1"),sQuery(id+"F32.wireOp",EDGE,"E100.2"),sQuery(id+"F32.wireOp",EDGE,"E100.3"),sQuery(id+"F32.wireOp",EDGE,"E100.4"),sQuery(id+"F32.wireOp",EDGE,"E100.5")])]}),"instanceName":"1"});
            var Q1;
            Q1=makeQuery(id+"F33.opExtrude","SWEPT_BODY",BODY,{"disambiguationData":[OSD([sQuery(id+"F32.wireOp",EDGE,"E94"),sQuery(id+"F32.wireOp",EDGE,"E95"),sQuery(id+"F32.wireOp",EDGE,"E96"),sQuery(id+"F32.wireOp",EDGE,"E97"),sQuery(id+"F32.wireOp",EDGE,"E100.0"),sQuery(id+"F32.wireOp",EDGE,"E100.1"),sQuery(id+"F32.wireOp",EDGE,"E100.2"),sQuery(id+"F32.wireOp",EDGE,"E100.3"),sQuery(id+"F32.wireOp",EDGE,"E100.4"),sQuery(id+"F32.wireOp",EDGE,"E100.5")])]});
            var Q2;
            Q2=qCreatedBy(id+"F37.planeOp",FACE);
            mirror(context, id + "F38", {"entities" : qUnion([Q0, Q1]), "mirrorPlane" : qUnion([Q2])});
        }
        {
            var Q0;
            Q0=makeQuery(id+"F38.opPattern","COPY",BODY,{"derivedFrom":makeQuery(id+"F33.opExtrude","SWEPT_BODY",BODY,{"disambiguationData":[OSD([sQuery(id+"F32.wireOp",EDGE,"E94"),sQuery(id+"F32.wireOp",EDGE,"E95"),sQuery(id+"F32.wireOp",EDGE,"E96"),sQuery(id+"F32.wireOp",EDGE,"E97"),sQuery(id+"F32.wireOp",EDGE,"E100.0"),sQuery(id+"F32.wireOp",EDGE,"E100.1"),sQuery(id+"F32.wireOp",EDGE,"E100.2"),sQuery(id+"F32.wireOp",EDGE,"E100.3"),sQuery(id+"F32.wireOp",EDGE,"E100.4"),sQuery(id+"F32.wireOp",EDGE,"E100.5")])]}),"instanceName":"1"});
            var Q1;
            Q1=makeQuery(id+"F38.opPattern","COPY",BODY,{"derivedFrom":makeQuery(id+"F36.opPattern","COPY",BODY,{"derivedFrom":makeQuery(id+"F33.opExtrude","SWEPT_BODY",BODY,{"disambiguationData":[OSD([sQuery(id+"F32.wireOp",EDGE,"E94"),sQuery(id+"F32.wireOp",EDGE,"E95"),sQuery(id+"F32.wireOp",EDGE,"E96"),sQuery(id+"F32.wireOp",EDGE,"E97"),sQuery(id+"F32.wireOp",EDGE,"E100.0"),sQuery(id+"F32.wireOp",EDGE,"E100.1"),sQuery(id+"F32.wireOp",EDGE,"E100.2"),sQuery(id+"F32.wireOp",EDGE,"E100.3"),sQuery(id+"F32.wireOp",EDGE,"E100.4"),sQuery(id+"F32.wireOp",EDGE,"E100.5")])]}),"instanceName":"1"}),"instanceName":"1"});
            var Q2;
            Q2=makeQuery(id+"F19.opExtrude","CAP_EDGE",EDGE,{"disambiguationData":[OSD([sQuery(id+"F18.wireOp",EDGE,"E56.0.2")])],"isStart":false});
            var Q3;
            Q3=makeQuery(id+"F19.opExtrude","CAP_EDGE",EDGE,{"disambiguationData":[OSD([sQuery(id+"F18.wireOp",EDGE,"E56.0.2")])],"isStart":false});
            transform(context, id + "F39", {"entities" : qUnion([Q0, Q1]), "transformType" : TransformType.TRANSLATION_ENTITY, "oppositeDirectionEntity" : false, "transformLine" : qUnion([Q2]), "makeCopy" : true});
        }
        {
            var Q0;
            Q0=makeQuery(id+"F39.opPattern","COPY",BODY,{"derivedFrom":makeQuery(id+"F38.opPattern","COPY",BODY,{"derivedFrom":makeQuery(id+"F36.opPattern","COPY",BODY,{"derivedFrom":makeQuery(id+"F33.opExtrude","SWEPT_BODY",BODY,{"disambiguationData":[OSD([sQuery(id+"F32.wireOp",EDGE,"E94"),sQuery(id+"F32.wireOp",EDGE,"E95"),sQuery(id+"F32.wireOp",EDGE,"E96"),sQuery(id+"F32.wireOp",EDGE,"E97"),sQuery(id+"F32.wireOp",EDGE,"E100.0"),sQuery(id+"F32.wireOp",EDGE,"E100.1"),sQuery(id+"F32.wireOp",EDGE,"E100.2"),sQuery(id+"F32.wireOp",EDGE,"E100.3"),sQuery(id+"F32.wireOp",EDGE,"E100.4"),sQuery(id+"F32.wireOp",EDGE,"E100.5")])]}),"instanceName":"1"}),"instanceName":"1"}),"instanceName":"1"});
            var Q1;
            Q1=makeQuery(id+"F39.opPattern","COPY",BODY,{"derivedFrom":makeQuery(id+"F38.opPattern","COPY",BODY,{"derivedFrom":makeQuery(id+"F33.opExtrude","SWEPT_BODY",BODY,{"disambiguationData":[OSD([sQuery(id+"F32.wireOp",EDGE,"E94"),sQuery(id+"F32.wireOp",EDGE,"E95"),sQuery(id+"F32.wireOp",EDGE,"E96"),sQuery(id+"F32.wireOp",EDGE,"E97"),sQuery(id+"F32.wireOp",EDGE,"E100.0"),sQuery(id+"F32.wireOp",EDGE,"E100.1"),sQuery(id+"F32.wireOp",EDGE,"E100.2"),sQuery(id+"F32.wireOp",EDGE,"E100.3"),sQuery(id+"F32.wireOp",EDGE,"E100.4"),sQuery(id+"F32.wireOp",EDGE,"E100.5")])]}),"instanceName":"1"}),"instanceName":"1"});
            var Q2;
            Q2=makeQuery(id+"F39.opPattern","COPY",EDGE,{"derivedFrom":makeQuery(id+"F38.opPattern","COPY",EDGE,{"derivedFrom":makeQuery(id+"F33.opExtrude","SWEPT_EDGE",EDGE,{"disambiguationData":[OSD([sQuery(id+"F20.wireOp",EDGE,"E66.top"),sQuery(id+"F20.wireOp",EDGE,"E66.left"),sQuery(id+"F32.wireOp",EDGE,"E94"),sQuery(id+"F32.wireOp",EDGE,"E97")])]}),"instanceName":"1"}),"instanceName":"1"});
            transform(context, id + "F40", {"entities" : qUnion([Q0, Q1]), "transformType" : TransformType.ROTATION, "transformAxis" : qUnion([Q2]), "angle" : 90 * degree, "makeCopy" : false});
        }
        {
            var Q0;
            Q0=makeQuery(id+"F19.opExtrude","SWEPT_BODY",BODY,{"disambiguationData":[OSD([sQuery(id+"F18.wireOp",EDGE,"E56.0.2"),sQuery(id+"F18.wireOp",EDGE,"E56.0.3"),sQuery(id+"F18.wireOp",EDGE,"E56.0.4"),sQuery(id+"F18.wireOp",EDGE,"E56.0.5"),sQuery(id+"F18.wireOp",EDGE,"E56.0.6"),sQuery(id+"F18.wireOp",EDGE,"E56.0.7"),sQuery(id+"F18.wireOp",EDGE,"E56.0.8"),sQuery(id+"F18.wireOp",EDGE,"E56.0.9"),sQuery(id+"F18.wireOp",EDGE,"E57"),sQuery(id+"F18.wireOp",EDGE,"E59"),sQuery(id+"F18.wireOp",EDGE,"E60"),sQuery(id+"F18.wireOp",EDGE,"E61.MirrorCS"),sQuery(id+"F18.wireOp",EDGE,"E62.MirrorCS"),sQuery(id+"F18.wireOp",EDGE,"E63.filletArc"),sQuery(id+"F18.wireOp",EDGE,"E64.filletArc")])]});
            var Q1;
            Q1=makeQuery(id+"F39.opPattern","COPY",BODY,{"derivedFrom":makeQuery(id+"F38.opPattern","COPY",BODY,{"derivedFrom":makeQuery(id+"F36.opPattern","COPY",BODY,{"derivedFrom":makeQuery(id+"F33.opExtrude","SWEPT_BODY",BODY,{"disambiguationData":[OSD([sQuery(id+"F32.wireOp",EDGE,"E94"),sQuery(id+"F32.wireOp",EDGE,"E95"),sQuery(id+"F32.wireOp",EDGE,"E96"),sQuery(id+"F32.wireOp",EDGE,"E97"),sQuery(id+"F32.wireOp",EDGE,"E100.0"),sQuery(id+"F32.wireOp",EDGE,"E100.1"),sQuery(id+"F32.wireOp",EDGE,"E100.2"),sQuery(id+"F32.wireOp",EDGE,"E100.3"),sQuery(id+"F32.wireOp",EDGE,"E100.4"),sQuery(id+"F32.wireOp",EDGE,"E100.5")])]}),"instanceName":"1"}),"instanceName":"1"}),"instanceName":"1"});
            var Q2;
            Q2=makeQuery(id+"F39.opPattern","COPY",BODY,{"derivedFrom":makeQuery(id+"F38.opPattern","COPY",BODY,{"derivedFrom":makeQuery(id+"F33.opExtrude","SWEPT_BODY",BODY,{"disambiguationData":[OSD([sQuery(id+"F32.wireOp",EDGE,"E94"),sQuery(id+"F32.wireOp",EDGE,"E95"),sQuery(id+"F32.wireOp",EDGE,"E96"),sQuery(id+"F32.wireOp",EDGE,"E97"),sQuery(id+"F32.wireOp",EDGE,"E100.0"),sQuery(id+"F32.wireOp",EDGE,"E100.1"),sQuery(id+"F32.wireOp",EDGE,"E100.2"),sQuery(id+"F32.wireOp",EDGE,"E100.3"),sQuery(id+"F32.wireOp",EDGE,"E100.4"),sQuery(id+"F32.wireOp",EDGE,"E100.5")])]}),"instanceName":"1"}),"instanceName":"1"});
            var Q3;
            Q3=makeQuery(id+"F38.opPattern","COPY",BODY,{"derivedFrom":makeQuery(id+"F33.opExtrude","SWEPT_BODY",BODY,{"disambiguationData":[OSD([sQuery(id+"F32.wireOp",EDGE,"E94"),sQuery(id+"F32.wireOp",EDGE,"E95"),sQuery(id+"F32.wireOp",EDGE,"E96"),sQuery(id+"F32.wireOp",EDGE,"E97"),sQuery(id+"F32.wireOp",EDGE,"E100.0"),sQuery(id+"F32.wireOp",EDGE,"E100.1"),sQuery(id+"F32.wireOp",EDGE,"E100.2"),sQuery(id+"F32.wireOp",EDGE,"E100.3"),sQuery(id+"F32.wireOp",EDGE,"E100.4"),sQuery(id+"F32.wireOp",EDGE,"E100.5")])]}),"instanceName":"1"});
            var Q4;
            Q4=makeQuery(id+"F38.opPattern","COPY",BODY,{"derivedFrom":makeQuery(id+"F36.opPattern","COPY",BODY,{"derivedFrom":makeQuery(id+"F33.opExtrude","SWEPT_BODY",BODY,{"disambiguationData":[OSD([sQuery(id+"F32.wireOp",EDGE,"E94"),sQuery(id+"F32.wireOp",EDGE,"E95"),sQuery(id+"F32.wireOp",EDGE,"E96"),sQuery(id+"F32.wireOp",EDGE,"E97"),sQuery(id+"F32.wireOp",EDGE,"E100.0"),sQuery(id+"F32.wireOp",EDGE,"E100.1"),sQuery(id+"F32.wireOp",EDGE,"E100.2"),sQuery(id+"F32.wireOp",EDGE,"E100.3"),sQuery(id+"F32.wireOp",EDGE,"E100.4"),sQuery(id+"F32.wireOp",EDGE,"E100.5")])]}),"instanceName":"1"}),"instanceName":"1"});
            var Q5;
            Q5=makeQuery(id+"F36.opPattern","COPY",BODY,{"derivedFrom":makeQuery(id+"F33.opExtrude","SWEPT_BODY",BODY,{"disambiguationData":[OSD([sQuery(id+"F32.wireOp",EDGE,"E94"),sQuery(id+"F32.wireOp",EDGE,"E95"),sQuery(id+"F32.wireOp",EDGE,"E96"),sQuery(id+"F32.wireOp",EDGE,"E97"),sQuery(id+"F32.wireOp",EDGE,"E100.0"),sQuery(id+"F32.wireOp",EDGE,"E100.1"),sQuery(id+"F32.wireOp",EDGE,"E100.2"),sQuery(id+"F32.wireOp",EDGE,"E100.3"),sQuery(id+"F32.wireOp",EDGE,"E100.4"),sQuery(id+"F32.wireOp",EDGE,"E100.5")])]}),"instanceName":"1"});
            var Q6;
            Q6=makeQuery(id+"F33.opExtrude","SWEPT_BODY",BODY,{"disambiguationData":[OSD([sQuery(id+"F32.wireOp",EDGE,"E94"),sQuery(id+"F32.wireOp",EDGE,"E95"),sQuery(id+"F32.wireOp",EDGE,"E96"),sQuery(id+"F32.wireOp",EDGE,"E97"),sQuery(id+"F32.wireOp",EDGE,"E100.0"),sQuery(id+"F32.wireOp",EDGE,"E100.1"),sQuery(id+"F32.wireOp",EDGE,"E100.2"),sQuery(id+"F32.wireOp",EDGE,"E100.3"),sQuery(id+"F32.wireOp",EDGE,"E100.4"),sQuery(id+"F32.wireOp",EDGE,"E100.5")])]});
            booleanBodies(context, id + "F41", {"operationType" : BooleanOperationType.UNION, "tools" : qUnion([Q0, Q1, Q2, Q3, Q4, Q5, Q6])});
        }
    });
